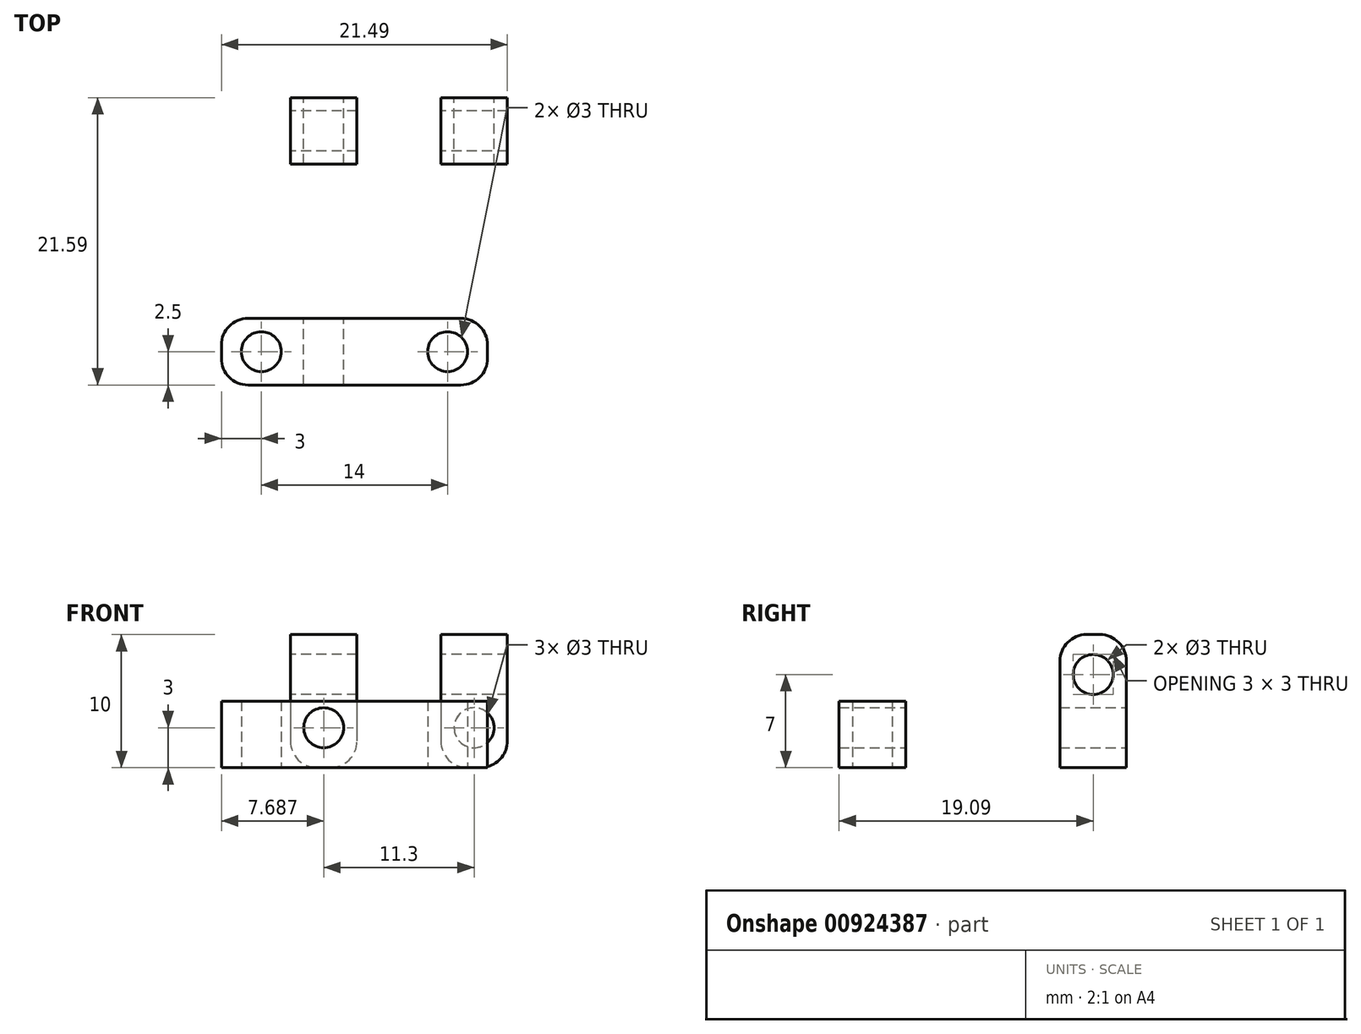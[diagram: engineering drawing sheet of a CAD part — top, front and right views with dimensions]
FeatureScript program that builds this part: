
annotation { "Feature Type Name" : "Feature", "Feature Type Description" : "" }
export const myFeature = defineFeature(function(context is Context, id is Id, definition is map)
    precondition{}
    {
        {
            var Q0;
            Q0=qCreatedBy(makeId("Top.planeOp"),FACE);
            var sketch = newSketch(context, id + "F0", { "sketchPlane" : qUnion([Q0])});
            skLineSegment(sketch, "E0.bottom", {"start": v(2, 0) * mm, "end": v(18, 0) * mm});
            skLineSegment(sketch, "E0.top", {"start": v(2, -5) * mm, "end": v(18, -5) * mm});
            skLineSegment(sketch, "E0.left", {"start": v(0, -2) * mm, "end": v(0, -3) * mm});
            skLineSegment(sketch, "E0.right", {"start": v(20, -2) * mm, "end": v(20, -3) * mm});
            skCircle(sketch, "E1", {"center": v(3, -2.5) * mm, "radius": 1.5 * mm});
            skPoint(sketch, "E1.centerSnap0", {"position": v(0, -2.5) * mm});
            skCircle(sketch, "E2", {"center": v(17, -2.5) * mm, "radius": 1.5 * mm});
            skPoint(sketch, "E2.centerSnap0", {"position": v(20, -2.5) * mm});
            skPoint(sketch, "E3.visualSharp", {"position": v(0, 0) * mm});
            skArc(sketch, "E3.filletArc", {"start": v(2, 0) * mm, "mid": v(0.59, -0.59) * mm, "end": v(0, -2) * mm});
            skPoint(sketch, "E4.visualSharp", {"position": v(0, -5) * mm});
            skArc(sketch, "E4.filletArc", {"start": v(0, -3) * mm, "mid": v(0.59, -4.41) * mm, "end": v(2, -5) * mm});
            skPoint(sketch, "E5.visualSharp", {"position": v(20, -5) * mm});
            skArc(sketch, "E5.filletArc", {"start": v(18, -5) * mm, "mid": v(19.41, -4.41) * mm, "end": v(20, -3) * mm});
            skPoint(sketch, "E6.visualSharp", {"position": v(20, 0) * mm});
            skArc(sketch, "E6.filletArc", {"start": v(20, -2) * mm, "mid": v(19.41, -0.59) * mm, "end": v(18, 0) * mm});
            skSolve(sketch);
        }
        {
            var Q0;
            Q0=makeQuery(id+"F0.imprint","IMPRINT",FACE,{"disambiguationData":[TD([[makeQuery(id+"F0.imprint","IMPRINT",EDGE,{"derivedFrom":sQuery(id+"F0.wireOp",EDGE,"E0.bottom")}),-1.0]])]});
            extrude(context, id + "F1", {"entities" : qUnion([Q0]), "depth" : 5 * mm, "offsetDistance" : 25 * mm});
        }
        {
            var Q0;
            Q0=qCreatedBy(makeId("Top.planeOp"),FACE);
            var sketch = newSketch(context, id + "F2", { "sketchPlane" : qUnion([Q0])});
            skLineSegment(sketch, "E7.bottom", {"start": v(5.19, 16.6) * mm, "end": v(10.19, 16.6) * mm});
            skLineSegment(sketch, "E7.top", {"start": v(5.19, 11.6) * mm, "end": v(10.19, 11.6) * mm});
            skLineSegment(sketch, "E7.left", {"start": v(5.19, 16.6) * mm, "end": v(5.19, 11.6) * mm});
            skLineSegment(sketch, "E7.right", {"start": v(10.19, 16.6) * mm, "end": v(10.19, 11.6) * mm});
            skSolve(sketch);
        }
        {
            var Q0;
            Q0=makeQuery(id+"F2.imprint","IMPRINT",FACE,{"disambiguationData":[TD([[makeQuery(id+"F2.imprint","IMPRINT",EDGE,{"derivedFrom":sQuery(id+"F2.wireOp",EDGE,"E7.bottom")}),-1.0]])]});
            extrude(context, id + "F3", {"entities" : qUnion([Q0]), "depth" : 10 * mm, "offsetDistance" : 25 * mm});
        }
        {
            var Q0;
            Q0=makeQuery(id+"F3.opExtrude","SWEPT_FACE",FACE,{"disambiguationData":[OSD([sQuery(id+"F2.wireOp",EDGE,"E7.left")])]});
            var sketch = newSketch(context, id + "F4", { "sketchPlane" : qUnion([Q0])});
            skCircle(sketch, "E8", {"center": v(-14.1, 7) * mm, "radius": 1.5 * mm});
            skPoint(sketch, "E8.centerSnap0", {"position": v(-14.1, 10) * mm});
            skSolve(sketch);
        }
        {
            var Q0;
            Q0=makeQuery(id+"F3.opExtrude","SWEPT_FACE",FACE,{"disambiguationData":[OSD([sQuery(id+"F2.wireOp",EDGE,"E7.bottom")])]});
            var sketch = newSketch(context, id + "F5", { "sketchPlane" : qUnion([Q0])});
            skCircle(sketch, "E9", {"center": v(-7.69, 3) * mm, "radius": 1.5 * mm});
            skPoint(sketch, "E9.centerSnap0", {"position": v(-7.69, 0) * mm});
            skSolve(sketch);
        }
        {
            var Q0;
            Q0 = qSketchRegion(id + "F5", true);
            extrude(context, id + "F6", {"entities" : qUnion([Q0]), "operationType" : NewBodyOperationType.REMOVE, "oppositeDirection" : true, "depth" : 25 * mm, "offsetDistance" : 25 * mm});
        }
        {
            var Q0;
            Q0=makeQuery(id+"F4.imprint","IMPRINT",FACE,{"disambiguationData":[TD([[makeQuery(id+"F4.imprint","IMPRINT",EDGE,{"derivedFrom":sQuery(id+"F4.wireOp",EDGE,"E8")}),1.0]])]});
            extrude(context, id + "F7", {"entities" : qUnion([Q0]), "operationType" : NewBodyOperationType.REMOVE, "oppositeDirection" : true, "depth" : 25 * mm, "offsetDistance" : 25 * mm});
        }
        {
            var Q0;
            Q0=makeQuery(id+"F3.opExtrude","CAP_EDGE",EDGE,{"disambiguationData":[OSD([sQuery(id+"F2.wireOp",EDGE,"E7.bottom")])],"isStart":false});
            var Q1;
            Q1=makeQuery(id+"F3.opExtrude","CAP_EDGE",EDGE,{"disambiguationData":[OSD([sQuery(id+"F2.wireOp",EDGE,"E7.top")])],"isStart":false});
            var Q2;
            Q2=makeQuery(id+"F3.opExtrude","CAP_EDGE",EDGE,{"disambiguationData":[OSD([sQuery(id+"F2.wireOp",EDGE,"E7.left")])],"isStart":true});
            var Q3;
            Q3=makeQuery(id+"F3.opExtrude","CAP_EDGE",EDGE,{"disambiguationData":[OSD([sQuery(id+"F2.wireOp",EDGE,"E7.right")])],"isStart":true});
            fillet(context, id + "F8", {"entities" : qUnion([Q0, Q1, Q2, Q3]), "radius" : 2 * mm, "tangentPropagation" : true, "allowEdgeOverflow" : false});
        }
        {
            var Q0;
            Q0=makeQuery(id+"F3.opExtrude","SWEPT_BODY",BODY,{"disambiguationData":[OSD([sQuery(id+"F2.wireOp",EDGE,"E7.bottom"),sQuery(id+"F2.wireOp",EDGE,"E7.top"),sQuery(id+"F2.wireOp",EDGE,"E7.left"),sQuery(id+"F2.wireOp",EDGE,"E7.right")])]});
            transform(context, id + "F9", {"entities" : qUnion([Q0]), "transformType" : TransformType.TRANSLATION_3D, "dx" : 11.3 * mm, "dy" : 0 * mm, "dz" : 0 * mm, "makeCopy" : true});
        }
    });
